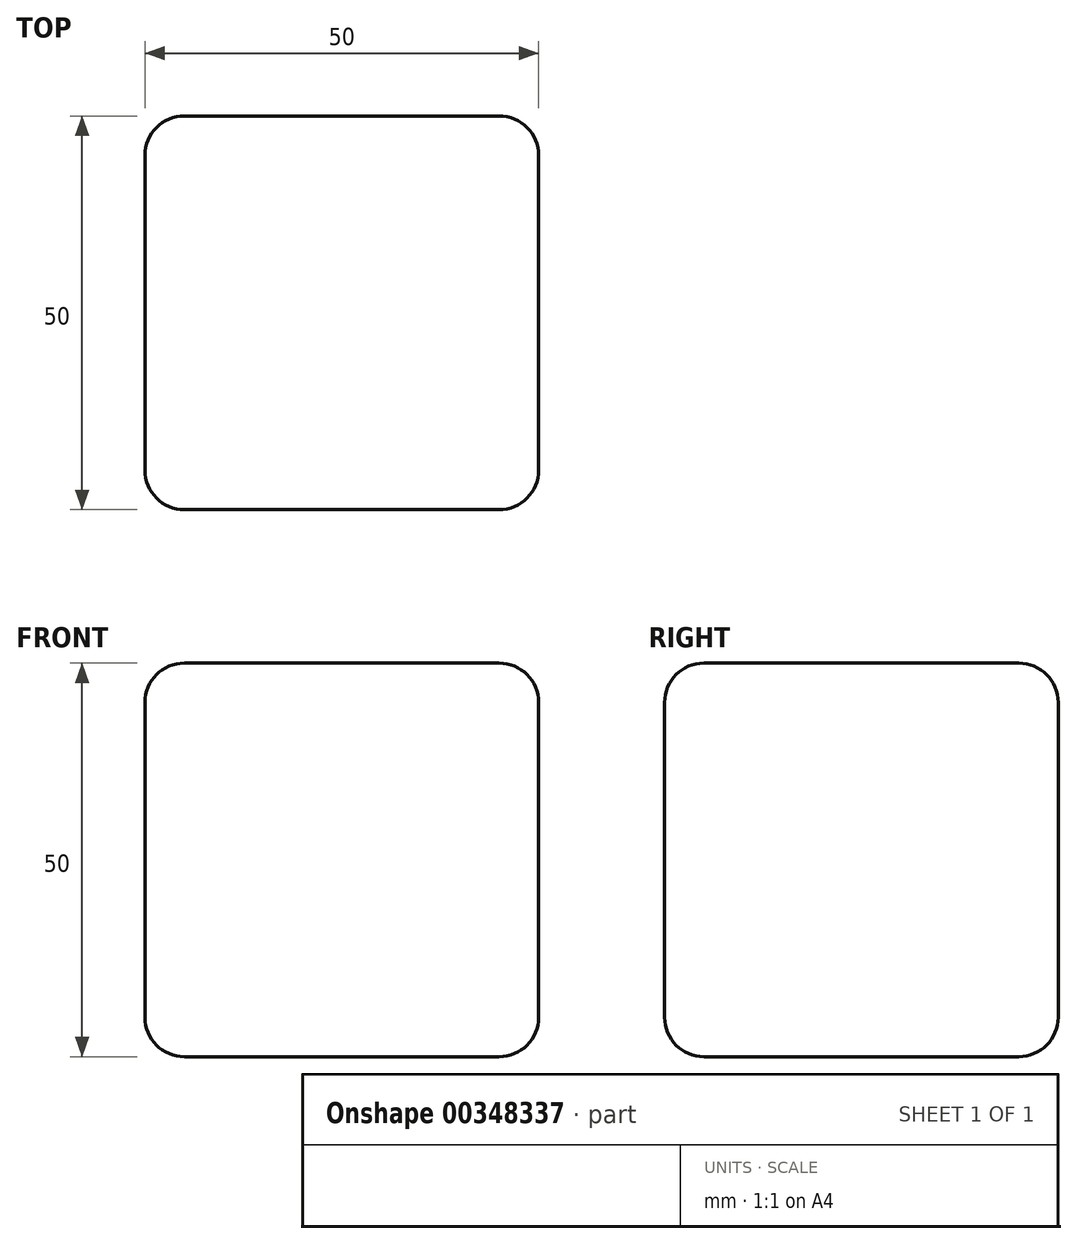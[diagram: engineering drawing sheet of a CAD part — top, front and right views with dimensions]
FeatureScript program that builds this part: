
annotation { "Feature Type Name" : "Feature", "Feature Type Description" : "" }
export const myFeature = defineFeature(function(context is Context, id is Id, definition is map)
    precondition{}
    {
        {
            var Q0;
            Q0=qCreatedBy(makeId("Front.planeOp"),FACE);
            var sketch = newSketch(context, id + "F0", { "sketchPlane" : qUnion([Q0])});
            skLineSegment(sketch, "E0.bottom", {"start": v(0, 0) * mm, "end": v(50, 0) * mm});
            skLineSegment(sketch, "E0.top", {"start": v(0, -50) * mm, "end": v(50, -50) * mm});
            skLineSegment(sketch, "E0.left", {"start": v(0, 0) * mm, "end": v(0, -50) * mm});
            skLineSegment(sketch, "E0.right", {"start": v(50, 0) * mm, "end": v(50, -50) * mm});
            skSolve(sketch);
        }
        {
            var Q0;
            Q0 = qSketchRegion(id + "F0", true);
            extrude(context, id + "F1", {"entities" : qUnion([Q0]), "depth" : 50 * mm});
        }
        {
            var Q0;
            Q0=makeQuery(id+"F1.opExtrude","SWEPT_FACE",FACE,{"disambiguationData":[OSD([sQuery(id+"F0.wireOp",EDGE,"E0.right")])]});
            var Q1;
            Q1=makeQuery(id+"F1.opExtrude","CAP_EDGE",EDGE,{"disambiguationData":[OSD([sQuery(id+"F0.wireOp",EDGE,"E0.left")])],"isStart":true});
            var Q2;
            Q2=makeQuery(id+"F1.opExtrude","SWEPT_FACE",FACE,{"disambiguationData":[OSD([sQuery(id+"F0.wireOp",EDGE,"E0.left")])]});
            var Q3;
            Q3=makeQuery(id+"F1.opExtrude","SWEPT_FACE",FACE,{"disambiguationData":[OSD([sQuery(id+"F0.wireOp",EDGE,"E0.top")])]});
            var Q4;
            Q4=makeQuery(id+"F1.opExtrude","CAP_FACE",FACE,{"disambiguationData":[OSD([sQuery(id+"F0.wireOp",EDGE,"E0.bottom"),sQuery(id+"F0.wireOp",EDGE,"E0.top"),sQuery(id+"F0.wireOp",EDGE,"E0.left"),sQuery(id+"F0.wireOp",EDGE,"E0.right")])],"isStart":false});
            var Q5;
            Q5=makeQuery(id+"F1.opExtrude","CAP_FACE",FACE,{"disambiguationData":[OSD([sQuery(id+"F0.wireOp",EDGE,"E0.bottom"),sQuery(id+"F0.wireOp",EDGE,"E0.top"),sQuery(id+"F0.wireOp",EDGE,"E0.left"),sQuery(id+"F0.wireOp",EDGE,"E0.right")])],"isStart":true});
            fillet(context, id + "F2", {"entities" : qUnion([Q0, Q1, Q2, Q3, Q4, Q5]), "radius" : 5 * mm, "tangentPropagation" : true, "allowEdgeOverflow" : false});
        }
    });
